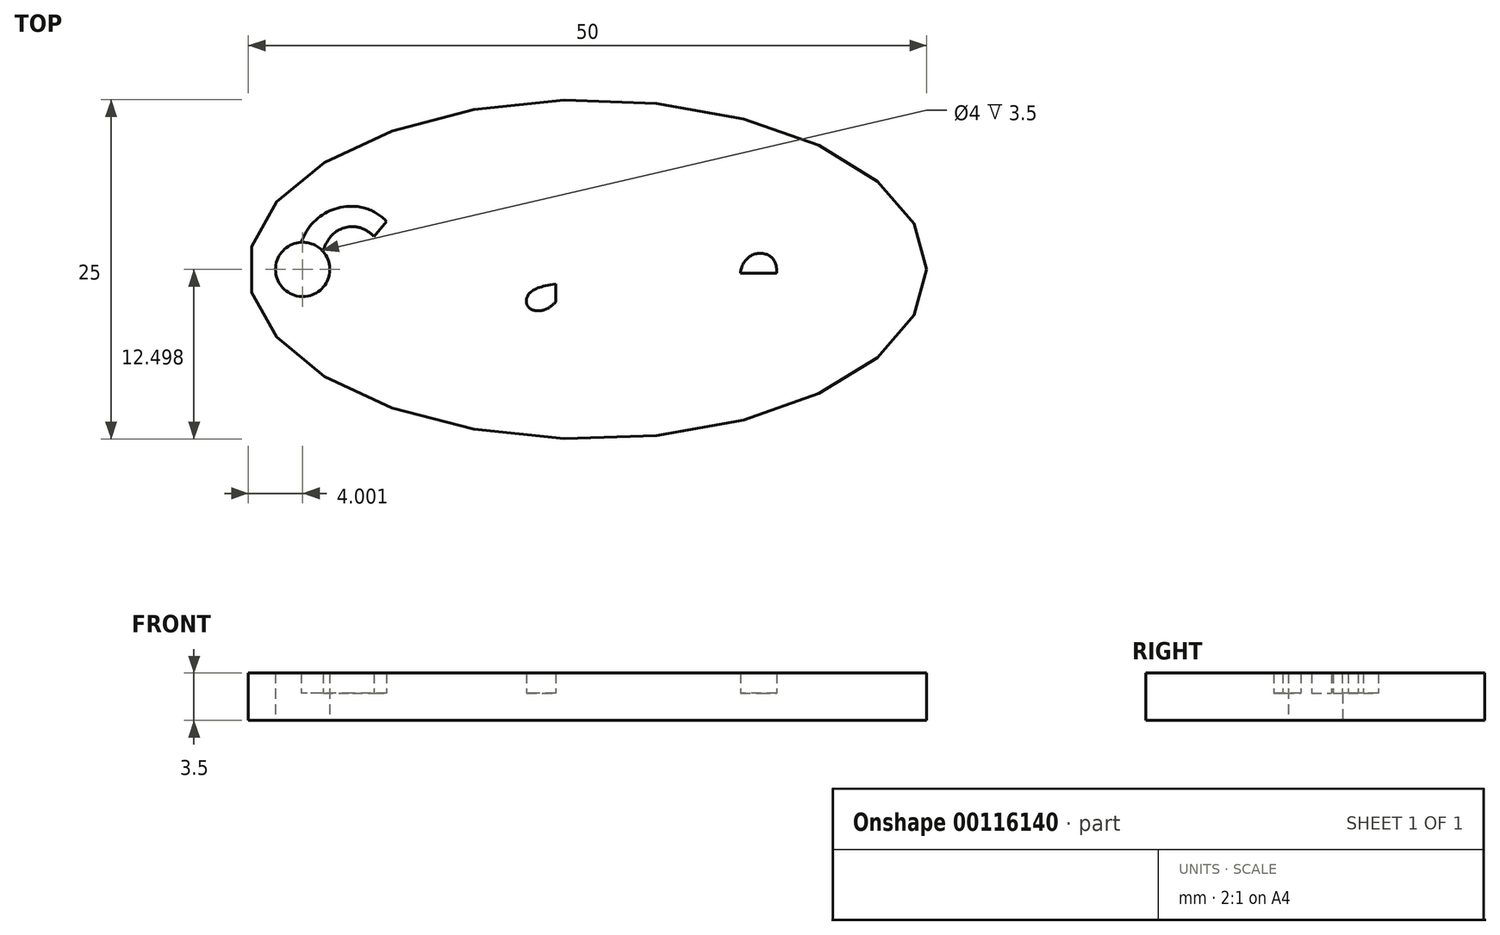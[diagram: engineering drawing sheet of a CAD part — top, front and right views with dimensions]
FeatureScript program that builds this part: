
annotation { "Feature Type Name" : "Feature", "Feature Type Description" : "" }
export const myFeature = defineFeature(function(context is Context, id is Id, definition is map)
    precondition{}
    {
        {
            var Q0;
            Q0=qCreatedBy(makeId("Top.planeOp"),FACE);
            var sketch = newSketch(context, id + "F0", { "sketchPlane" : qUnion([Q0])});
            skEllipse(sketch, "E0", {"center": v(-39.52, 12.23) * mm, "majorRadius": 25 * mm, "minorRadius": 12.5 * mm, "majorAxis": v(1, 0)});
            skCircle(sketch, "E1", {"center": v(-60.52, 12.23) * mm, "radius": 2 * mm});
            skLineSegment(sketch, "E2", {"start": v(-64.52, 19.83) * mm, "end": v(-64.52, 5.96) * mm, "construction": true});
            skSolve(sketch);
        }
        {
            var Q0;
            Q0=makeQuery(id+"F0.imprint","IMPRINT",FACE,{"disambiguationData":[TD([[makeQuery(id+"F0.imprint","IMPRINT",EDGE,{"derivedFrom":sQuery(id+"F0.wireOp",EDGE,"E0")}),1.0]])]});
            extrude(context, id + "F1", {"entities" : qUnion([Q0]), "depth" : 2 * mm});
        }
        {
            var Q0;
            Q0=makeQuery(id+"F1.opExtrude","CAP_FACE",FACE,{"disambiguationData":[OSD([sQuery(id+"F0.wireOp",EDGE,"E0"),sQuery(id+"F0.wireOp",EDGE,"E1")])],"isStart":false});
            var sketch = newSketch(context, id + "F2", { "sketchPlane" : qUnion([Q0])});
            skText(sketch, "E3", { "text": "Charles", "fontName": "NotoSansCJKsc-Bold.otf"});
            skPoint(sketch, "E4.startSnap0", {"position": v(-64.52, 12.23) * mm});
            skPoint(sketch, "E5.endSnap0", {"position": v(-59, 12.23) * mm});
            skFitSpline(sketch, "E6.0", {"points": [v(-16.73, 10.55) * mm, v(-16.41, 12.23) * mm, v(-16.73, 13.9) * mm, v(-17.63, 15.42) * mm, v(-18.8, 16.66) * mm, v(-20.27, 17.89) * mm, v(-22.62, 19.32) * mm, v(-25.57, 20.54) * mm, v(-28.24, 21.34) * mm, v(-31.05, 22) * mm, v(-34.05, 22.46) * mm, v(-37.15, 22.69) * mm, v(-39.52, 22.75) * mm, v(-41.88, 22.69) * mm, v(-44.99, 22.46) * mm, v(-47.98, 22) * mm, v(-50.8, 21.34) * mm, v(-53.47, 20.54) * mm, v(-56.42, 19.32) * mm, v(-58.77, 17.89) * mm, v(-60.24, 16.66) * mm, v(-61.4, 15.42) * mm, v(-62.3, 13.9) * mm, v(-62.63, 12.23) * mm, v(-62.3, 10.55) * mm, v(-61.4, 9.04) * mm, v(-60.24, 7.8) * mm, v(-58.77, 6.57) * mm, v(-56.42, 5.13) * mm, v(-53.47, 3.92) * mm, v(-50.8, 3.12) * mm, v(-47.98, 2.45) * mm, v(-44.99, 2) * mm, v(-41.88, 1.77) * mm, v(-39.52, 1.7) * mm, v(-37.15, 1.77) * mm, v(-34.05, 2) * mm, v(-31.05, 2.45) * mm, v(-28.24, 3.12) * mm, v(-25.57, 3.92) * mm, v(-22.62, 5.13) * mm, v(-20.27, 6.57) * mm, v(-18.8, 7.8) * mm, v(-17.63, 9.04) * mm, v(-16.73, 10.55) * mm, v(-16.41, 12.23) * mm, v(-16.73, 13.9) * mm, v(-16.73, 10.55) * mm]});
            skLineSegment(sketch, "E7", {"start": v(-64.52, 12.23) * mm, "end": v(-14.52, 12.23) * mm, "construction": true});
            skLineSegment(sketch, "E8", {"start": v(-39.52, 24.73) * mm, "end": v(-39.52, -0.27) * mm, "construction": true});
            const initialGuessF2  = {"E3": [-0.06159, 0.00798, 1, 0, 0.0085]};
            skSetInitialGuess(sketch, initialGuessF2);
            skSolve(sketch);
        }
        {
            var Q0;
            Q0=makeQuery(id+"F2.imprint","IMPRINT",FACE,{"disambiguationData":[TD([[makeQuery(id+"F2.imprint","IMPRINT",EDGE,{"derivedFrom":sQuery(id+"F2.wireOp",EDGE,"E3.sketch_text.stroke-0")}),1.0]])]});
            var Q1;
            Q1=makeQuery(id+"F2.imprint","IMPRINT",FACE,{"disambiguationData":[TD([[makeQuery(id+"F2.imprint","IMPRINT",EDGE,{"derivedFrom":sQuery(id+"F2.wireOp",EDGE,"E3.sketch_text.stroke-10")}),1.0]])]});
            var Q2;
            Q2=makeQuery(id+"F2.imprint","IMPRINT",FACE,{"disambiguationData":[TD([[makeQuery(id+"F2.imprint","IMPRINT",EDGE,{"derivedFrom":sQuery(id+"F2.wireOp",EDGE,"E3.sketch_text.stroke-18")}),1.0]])]});
            var Q3;
            Q3=makeQuery(id+"F2.imprint","IMPRINT",FACE,{"disambiguationData":[TD([[makeQuery(id+"F2.imprint","IMPRINT",EDGE,{"derivedFrom":sQuery(id+"F2.wireOp",EDGE,"E3.sketch_text.stroke-30")}),1.0]])]});
            var Q4;
            Q4=makeQuery(id+"F2.imprint","IMPRINT",FACE,{"disambiguationData":[TD([[makeQuery(id+"F2.imprint","IMPRINT",EDGE,{"derivedFrom":makeQuery(id+"F1.opExtrude","CAP_EDGE",EDGE,{"disambiguationData":[OSD([sQuery(id+"F0.wireOp",EDGE,"E0")])],"isStart":false})}),1.0]])]});
            var Q5;
            Q5=makeQuery(id+"F2.imprint","IMPRINT",FACE,{"disambiguationData":[TD([[makeQuery(id+"F2.imprint","IMPRINT",EDGE,{"derivedFrom":sQuery(id+"F2.wireOp",EDGE,"E3.sketch_text.stroke-45")}),1.0]])]});
            var Q6;
            Q6=makeQuery(id+"F2.imprint","IMPRINT",FACE,{"disambiguationData":[TD([[makeQuery(id+"F2.imprint","IMPRINT",EDGE,{"derivedFrom":sQuery(id+"F2.wireOp",EDGE,"E3.sketch_text.stroke-58")}),1.0]])]});
            var Q7;
            Q7=makeQuery(id+"F2.imprint","IMPRINT",FACE,{"disambiguationData":[TD([[makeQuery(id+"F2.imprint","IMPRINT",EDGE,{"derivedFrom":sQuery(id+"F2.wireOp",EDGE,"E3.sketch_text.stroke-74")}),1.0]])]});
            var Q8;
            Q8=makeQuery(id+"F2.imprint","IMPRINT",FACE,{"disambiguationData":[TD([[makeQuery(id+"F2.imprint","IMPRINT",EDGE,{"derivedFrom":sQuery(id+"F2.wireOp",EDGE,"E3.sketch_text.stroke-78")}),1.0]])]});
            var Q9;
            Q9=makeQuery(id+"F2.imprint","IMPRINT",FACE,{"disambiguationData":[TD([[makeQuery(id+"F2.imprint","IMPRINT",EDGE,{"derivedFrom":sQuery(id+"F2.wireOp",EDGE,"E3.sketch_text.stroke-62")}),1.0]])]});
            var Q10;
            Q10=makeQuery(id+"F2.imprint","IMPRINT",FACE,{"disambiguationData":[TD([[makeQuery(id+"F2.imprint","IMPRINT",EDGE,{"derivedFrom":sQuery(id+"F2.wireOp",EDGE,"E3.sketch_text.stroke-50")}),1.0]])]});
            extrude(context, id + "F3", {"entities" : qUnion([Q0, Q1, Q2, Q3, Q4, Q5, Q6, Q7, Q8, Q9, Q10]), "operationType" : NewBodyOperationType.ADD, "depth" : 1.5 * mm});
        }
    });
